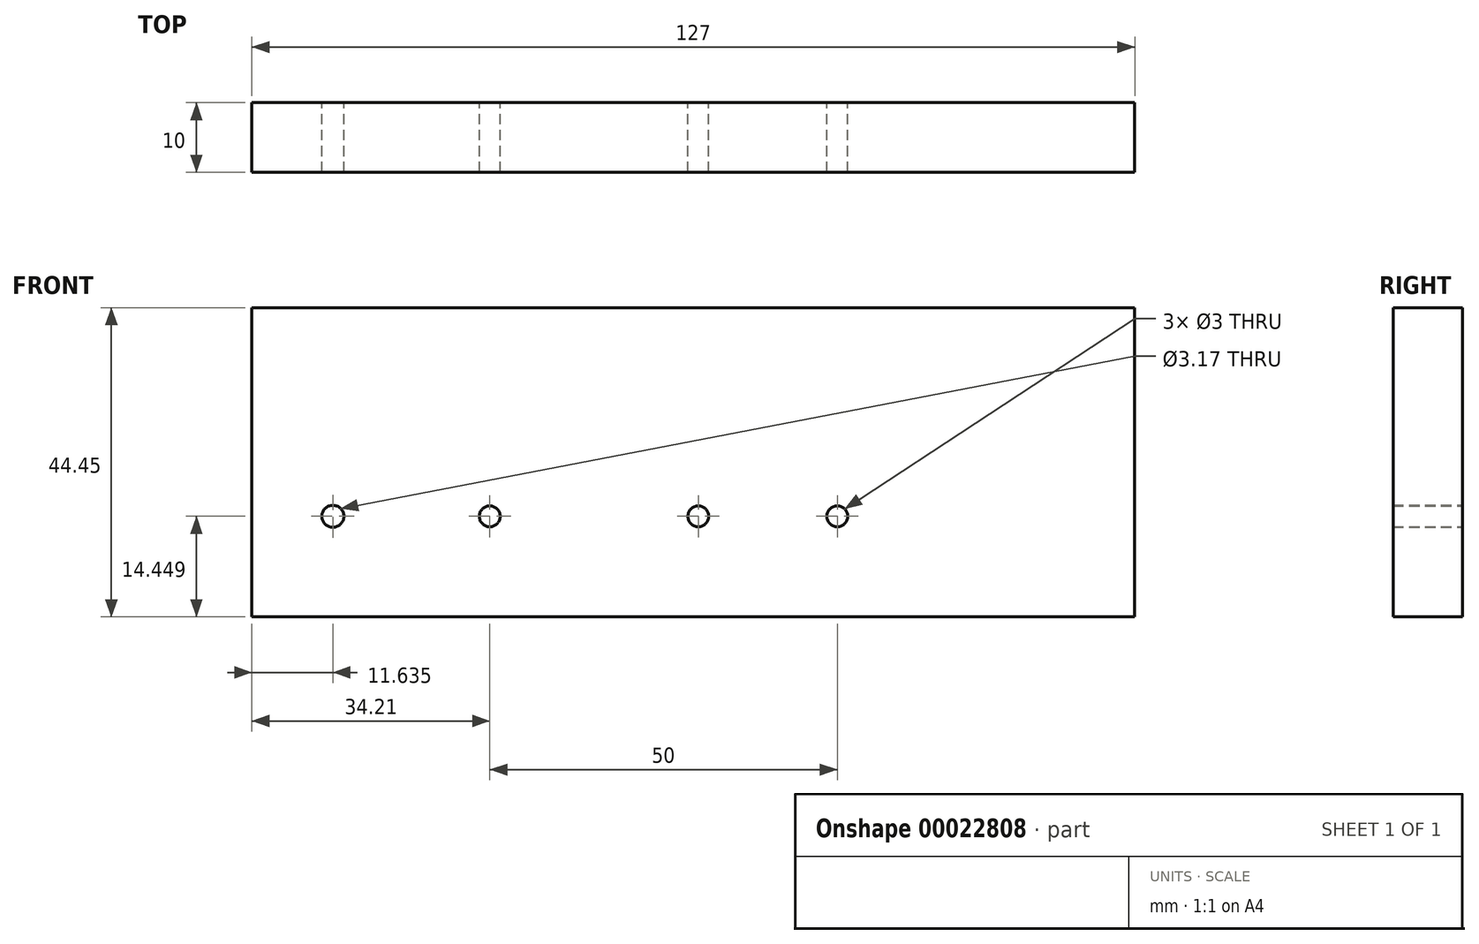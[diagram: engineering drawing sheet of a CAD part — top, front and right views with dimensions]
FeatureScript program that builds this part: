
annotation { "Feature Type Name" : "Feature", "Feature Type Description" : "" }
export const myFeature = defineFeature(function(context is Context, id is Id, definition is map)
    precondition{}
    {
        {
            var Q0;
            Q0=qCreatedBy(makeId("Front.planeOp"),FACE);
            var sketch = newSketch(context, id + "F0", { "sketchPlane" : qUnion([Q0])});
            skLineSegment(sketch, "E0.left", {"start": v(-64.32, 28.19) * mm, "end": v(-64.32, -16.26) * mm});
            skLineSegment(sketch, "E0.right", {"start": v(62.68, 28.19) * mm, "end": v(62.68, -16.26) * mm});
            skPoint(sketch, "E1.orphan", {"position": v(33.68, 0) * mm});
            skPoint(sketch, "E2.start.orphan", {"position": v(-32.7, 0) * mm});
            skPoint(sketch, "E3.trimOffspring.end.orphan", {"position": v(62.68, 5.96) * mm});
            skPoint(sketch, "E4.orphan", {"position": v(-64.32, -1.81) * mm});
            skLineSegment(sketch, "E5.trimOffspring", {"start": v(-10.11, -1.81) * mm, "end": v(-30.11, -1.81) * mm});
            skLineSegment(sketch, "E6", {"start": v(-10.11, -1.81) * mm, "end": v(-0.11, -1.81) * mm});
            skLineSegment(sketch, "E7", {"start": v(-30.11, -1.81) * mm, "end": v(-31.61, -1.81) * mm});
            skCircle(sketch, "E8", {"center": v(-30.11, -1.81) * mm, "radius": 1.5 * mm});
            skCircle(sketch, "E9", {"center": v(-0.11, -1.81) * mm, "radius": 1.5 * mm});
            skLineSegment(sketch, "E10", {"start": v(-0.11, -1.81) * mm, "end": v(19.89, -1.81) * mm});
            skCircle(sketch, "E11", {"center": v(19.89, -1.81) * mm, "radius": 1.5 * mm});
            skLineSegment(sketch, "E12", {"start": v(-64.32, 28.19) * mm, "end": v(62.68, 28.19) * mm});
            skCircle(sketch, "E13", {"center": v(-52.69, -1.81) * mm, "radius": 1.59 * mm});
            skLineSegment(sketch, "E14", {"start": v(62.68, -16.26) * mm, "end": v(-64.32, -16.26) * mm});
            skPoint(sketch, "E15.orphan", {"position": v(-64.32, -31.81) * mm});
            skSolve(sketch);
        }
        {
            var Q0;
            Q0=makeQuery(id+"F0.imprint","IMPRINT",FACE,{"disambiguationData":[TD([[makeQuery(id+"F0.imprint","IMPRINT",EDGE,{"derivedFrom":sQuery(id+"F0.wireOp",EDGE,"E0.left")}),1.0]])]});
            extrude(context, id + "F1", {"entities" : qUnion([Q0]), "depth" : 10 * mm});
        }
    });
